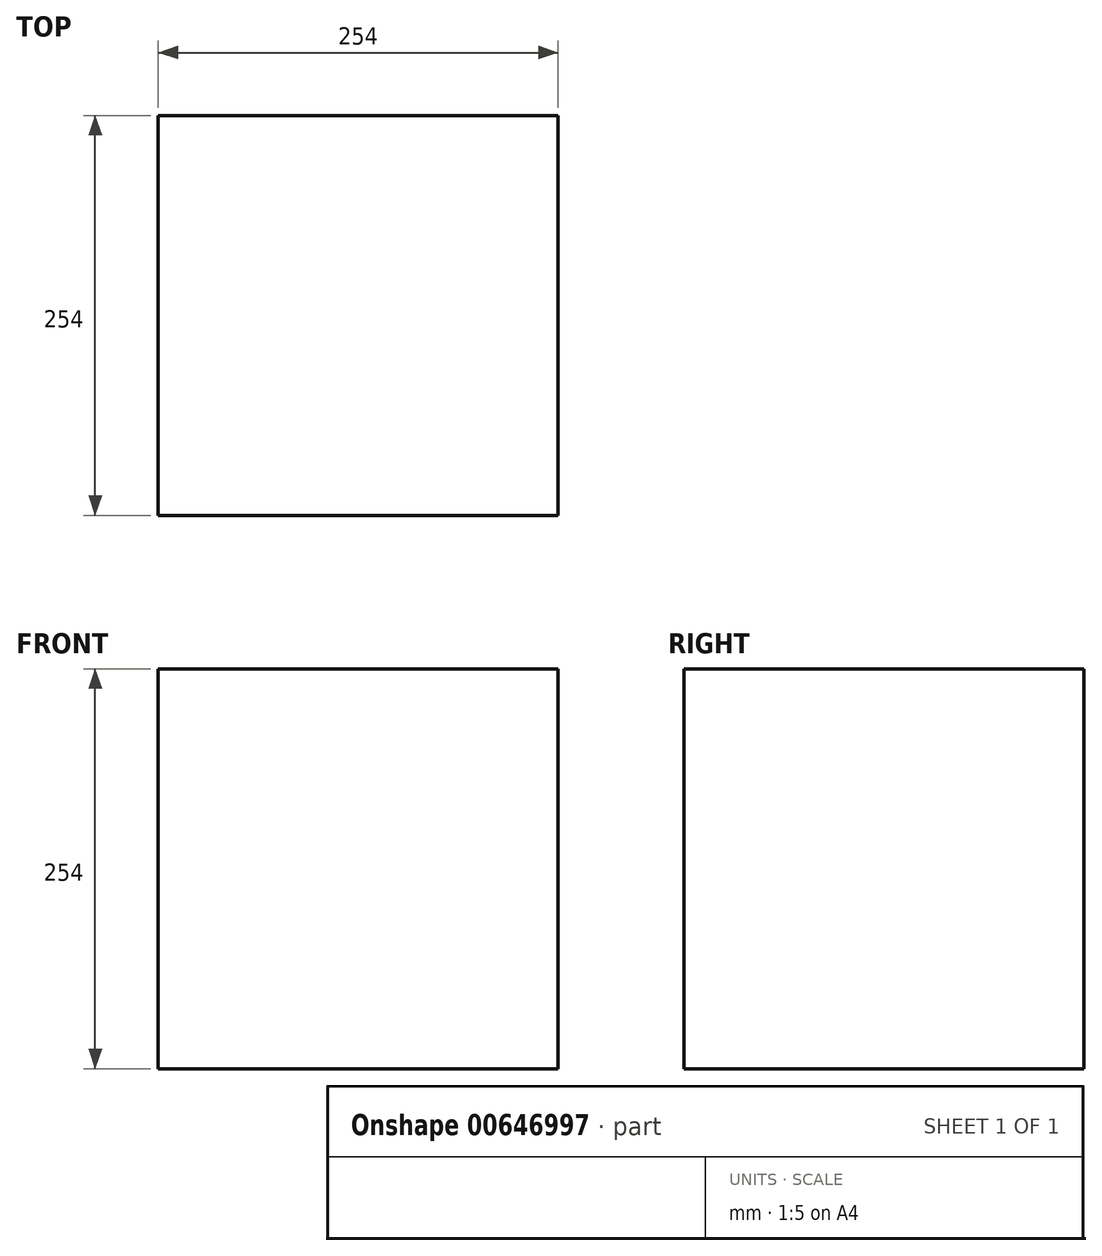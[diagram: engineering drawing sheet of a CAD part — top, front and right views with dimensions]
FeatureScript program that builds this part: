
annotation { "Feature Type Name" : "Feature", "Feature Type Description" : "" }
export const myFeature = defineFeature(function(context is Context, id is Id, definition is map)
    precondition{}
    {
        {
            var Q0;
            Q0=qCreatedBy(makeId("Front.planeOp"),FACE);
            var sketch = newSketch(context, id + "F0", { "sketchPlane" : qUnion([Q0])});
            skLineSegment(sketch, "E0.bottom", {"start": v(-131.46, 106.64) * mm, "end": v(122.54, 106.64) * mm});
            skLineSegment(sketch, "E0.top", {"start": v(-131.46, -147.36) * mm, "end": v(122.54, -147.36) * mm});
            skLineSegment(sketch, "E0.left", {"start": v(-131.46, 106.64) * mm, "end": v(-131.46, -147.36) * mm});
            skLineSegment(sketch, "E0.right", {"start": v(122.54, 106.64) * mm, "end": v(122.54, -147.36) * mm});
            skSolve(sketch);
        }
        {
            var Q0;
            Q0 = qSketchRegion(id + "F0", true);
            extrude(context, id + "F1", {"entities" : qUnion([Q0]), "endBound" : BoundingType.SYMMETRIC, "depth" : 254 * mm, "offsetDistance" : 25.4 * mm});
        }
    });
